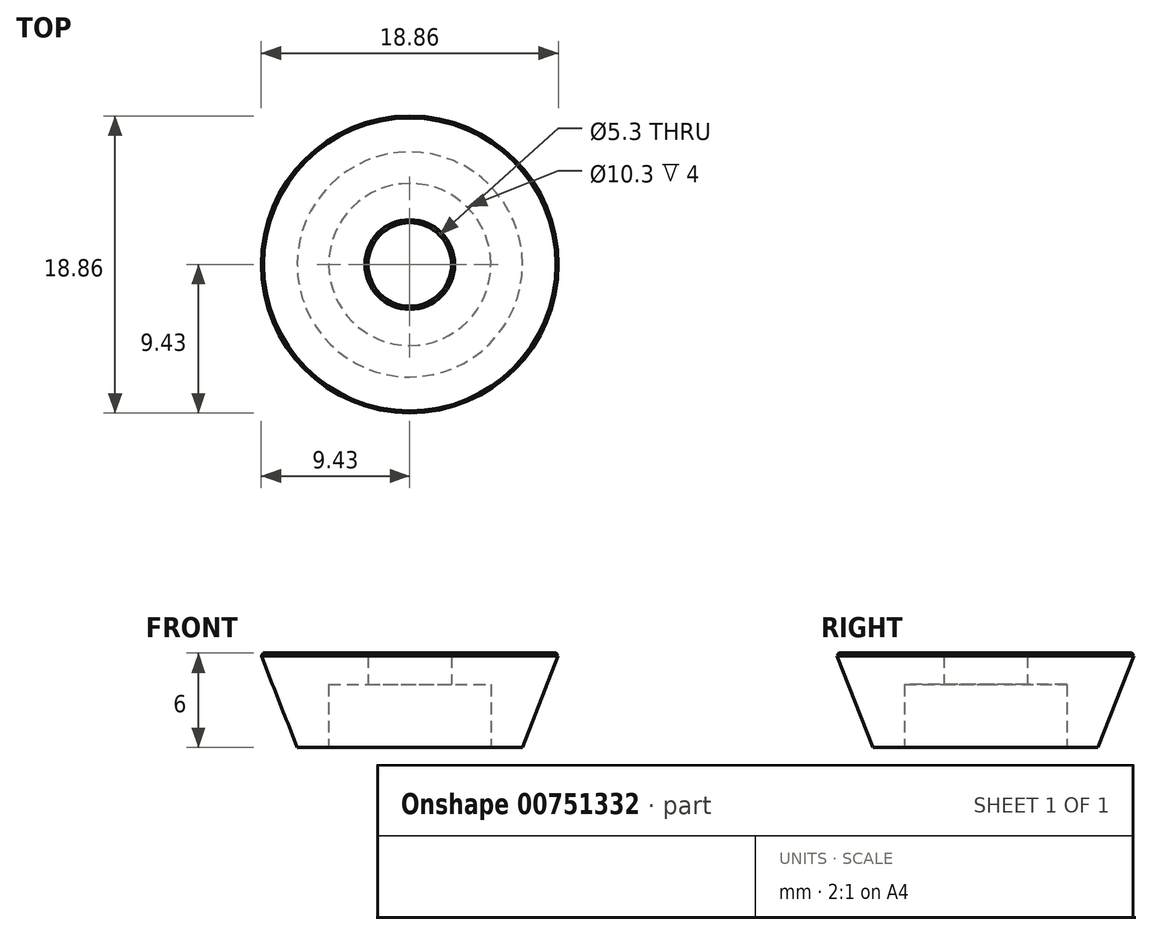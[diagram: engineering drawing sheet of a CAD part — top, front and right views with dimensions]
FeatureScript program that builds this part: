
annotation { "Feature Type Name" : "Feature", "Feature Type Description" : "" }
export const myFeature = defineFeature(function(context is Context, id is Id, definition is map)
    precondition{}
    {
        {
            var Q0;
            Q0=qCreatedBy(makeId("Front.planeOp"),FACE);
            var sketch = newSketch(context, id + "F0", { "sketchPlane" : qUnion([Q0]), "disableImprinting" : false});
            skLineSegment(sketch, "E0", {"start": v(-2.65, 6) * mm, "end": v(-2.65, 4) * mm});
            skLineSegment(sketch, "E1", {"start": v(-2.65, 4) * mm, "end": v(-5.15, 4) * mm});
            skLineSegment(sketch, "E2", {"start": v(-5.15, 4) * mm, "end": v(-5.15, 0) * mm});
            skLineSegment(sketch, "E3", {"start": v(-5.15, 0) * mm, "end": v(-7.15, 0) * mm});
            skLineSegment(sketch, "E4", {"start": v(-7.15, 0) * mm, "end": v(-9.5, 6) * mm});
            skLineSegment(sketch, "E5", {"start": v(-9.5, 6) * mm, "end": v(-2.65, 6) * mm});
            skLineSegment(sketch, "E6", {"start": v(0, 0) * mm, "end": v(0, 14.85) * mm});
            skSolve(sketch);
        }
        {
            var Q0;
            Q0 = qSketchRegion(id + "F0", true);
            var Q1;
            Q1=sQuery(id+"F0.wireOp",EDGE,"E6");
            revolve(context, id + "F1", {"surfaceOperationType" : NewSurfaceOperationType.NEW, "entities" : qUnion([Q0]), "axis" : qUnion([Q1]), "revolveType" : RevolveType.FULL});
        }
        {
            var Q0;
            Q0=makeQuery(id+"F1.opRevolve","SWEPT_FACE",FACE,{"disambiguationData":[OSD([sQuery(id+"F0.wireOp",EDGE,"E5")])]});
            chamfer(context, id + "F2", {"entities" : qUnion([Q0]), "width" : 0.2 * mm});
        }
    });
